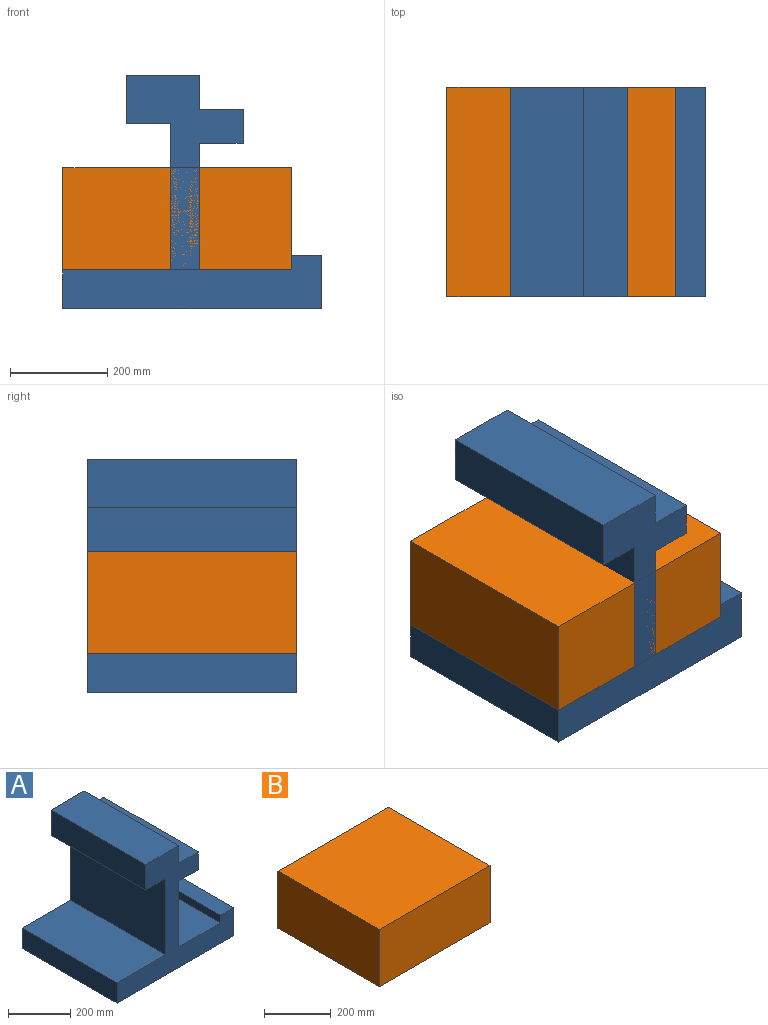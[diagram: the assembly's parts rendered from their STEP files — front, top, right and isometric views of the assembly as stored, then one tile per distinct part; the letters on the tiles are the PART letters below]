
ASSEMBLY  parts=2 mates=1
PART A: 18 faces, bbox 530x430x480 mm
  f0: plane 430x260mm, normal (1,0,0), area 111800mm2, adj f2,f4,f6,f13
  f1: plane 430x220mm, normal (0,0,1), area 94600mm2, adj f3,f4,f6,f10
  f2: plane 430x190mm, normal (0,0,1), area 81700mm2, adj f0,f4,f6,f8
  f3: plane 430x80mm, normal (-1,0,0), area 34400mm2, adj f1,f4,f6,f7
  f4: plane 530x480mm, normal (0,-1,0), area 83500mm2, adj f0,f1,f2,f3,f5,f7,f8,f9
  f5: plane 430x110mm, normal (1,0,0), area 47300mm2, adj f4,f6,f7,f9
  f6: plane 530x480mm, normal (0,1,0), area 83500mm2, adj f0,f1,f2,f3,f5,f7,f8,f9
  f7: plane 530x430mm, normal (0,0,-1), area 227900mm2, adj f3,f4,f5,f6
  f8: plane 430x30mm, normal (-1,0,0), area 12900mm2, adj f2,f4,f6,f9
  f9: plane 430x60mm, normal (0,0,1), area 25800mm2, adj f4,f5,f6,f8
  f10: plane 430x300mm, normal (-1,0,0), area 129000mm2, adj f1,f4,f6,f17
  f11: plane 430x70mm, normal (1,0,0), area 30100mm2, adj f4,f6,f12,f13
  f12: plane 430x90mm, normal (0,0,1), area 38700mm2, adj f4,f6,f11,f14
  f13: plane 430x90mm, normal (0,0,-1), area 38700mm2, adj f0,f4,f6,f11
  f14: plane 430x70mm, normal (1,0,0), area 30100mm2, adj f4,f6,f12,f16
  f15: plane 430x100mm, normal (-1,0,0), area 43000mm2, adj f4,f6,f16,f17
  f16: plane 430x150mm, normal (0,0,1), area 64500mm2, adj f4,f6,f14,f15
  f17: plane 430x90mm, normal (0,0,-1), area 38700mm2, adj f4,f6,f10,f15
PART B: 6 faces, bbox 470x430x210 mm
  f0: plane 430x210mm, normal (-1,0,0), area 90300mm2, adj f1,f3,f4,f5
  f1: plane 470x210mm, normal (0,-1,0), area 98700mm2, adj f0,f2,f4,f5
  f2: plane 430x210mm, normal (1,0,0), area 90300mm2, adj f1,f3,f4,f5
  f3: plane 470x210mm, normal (0,1,0), area 98700mm2, adj f0,f2,f4,f5
  f4: plane 470x430mm, normal (0,0,1), area 202100mm2, adj f0,f1,f2,f3
  f5: plane 470x430mm, normal (0,0,-1), area 202100mm2, adj f0,f1,f2,f3
PLACE A at identity
PLACE B t=(0,0,80)mm
MATE fastened B.f5 <-> A.f1  axis (0,0,1) through (0,0,80)mm
